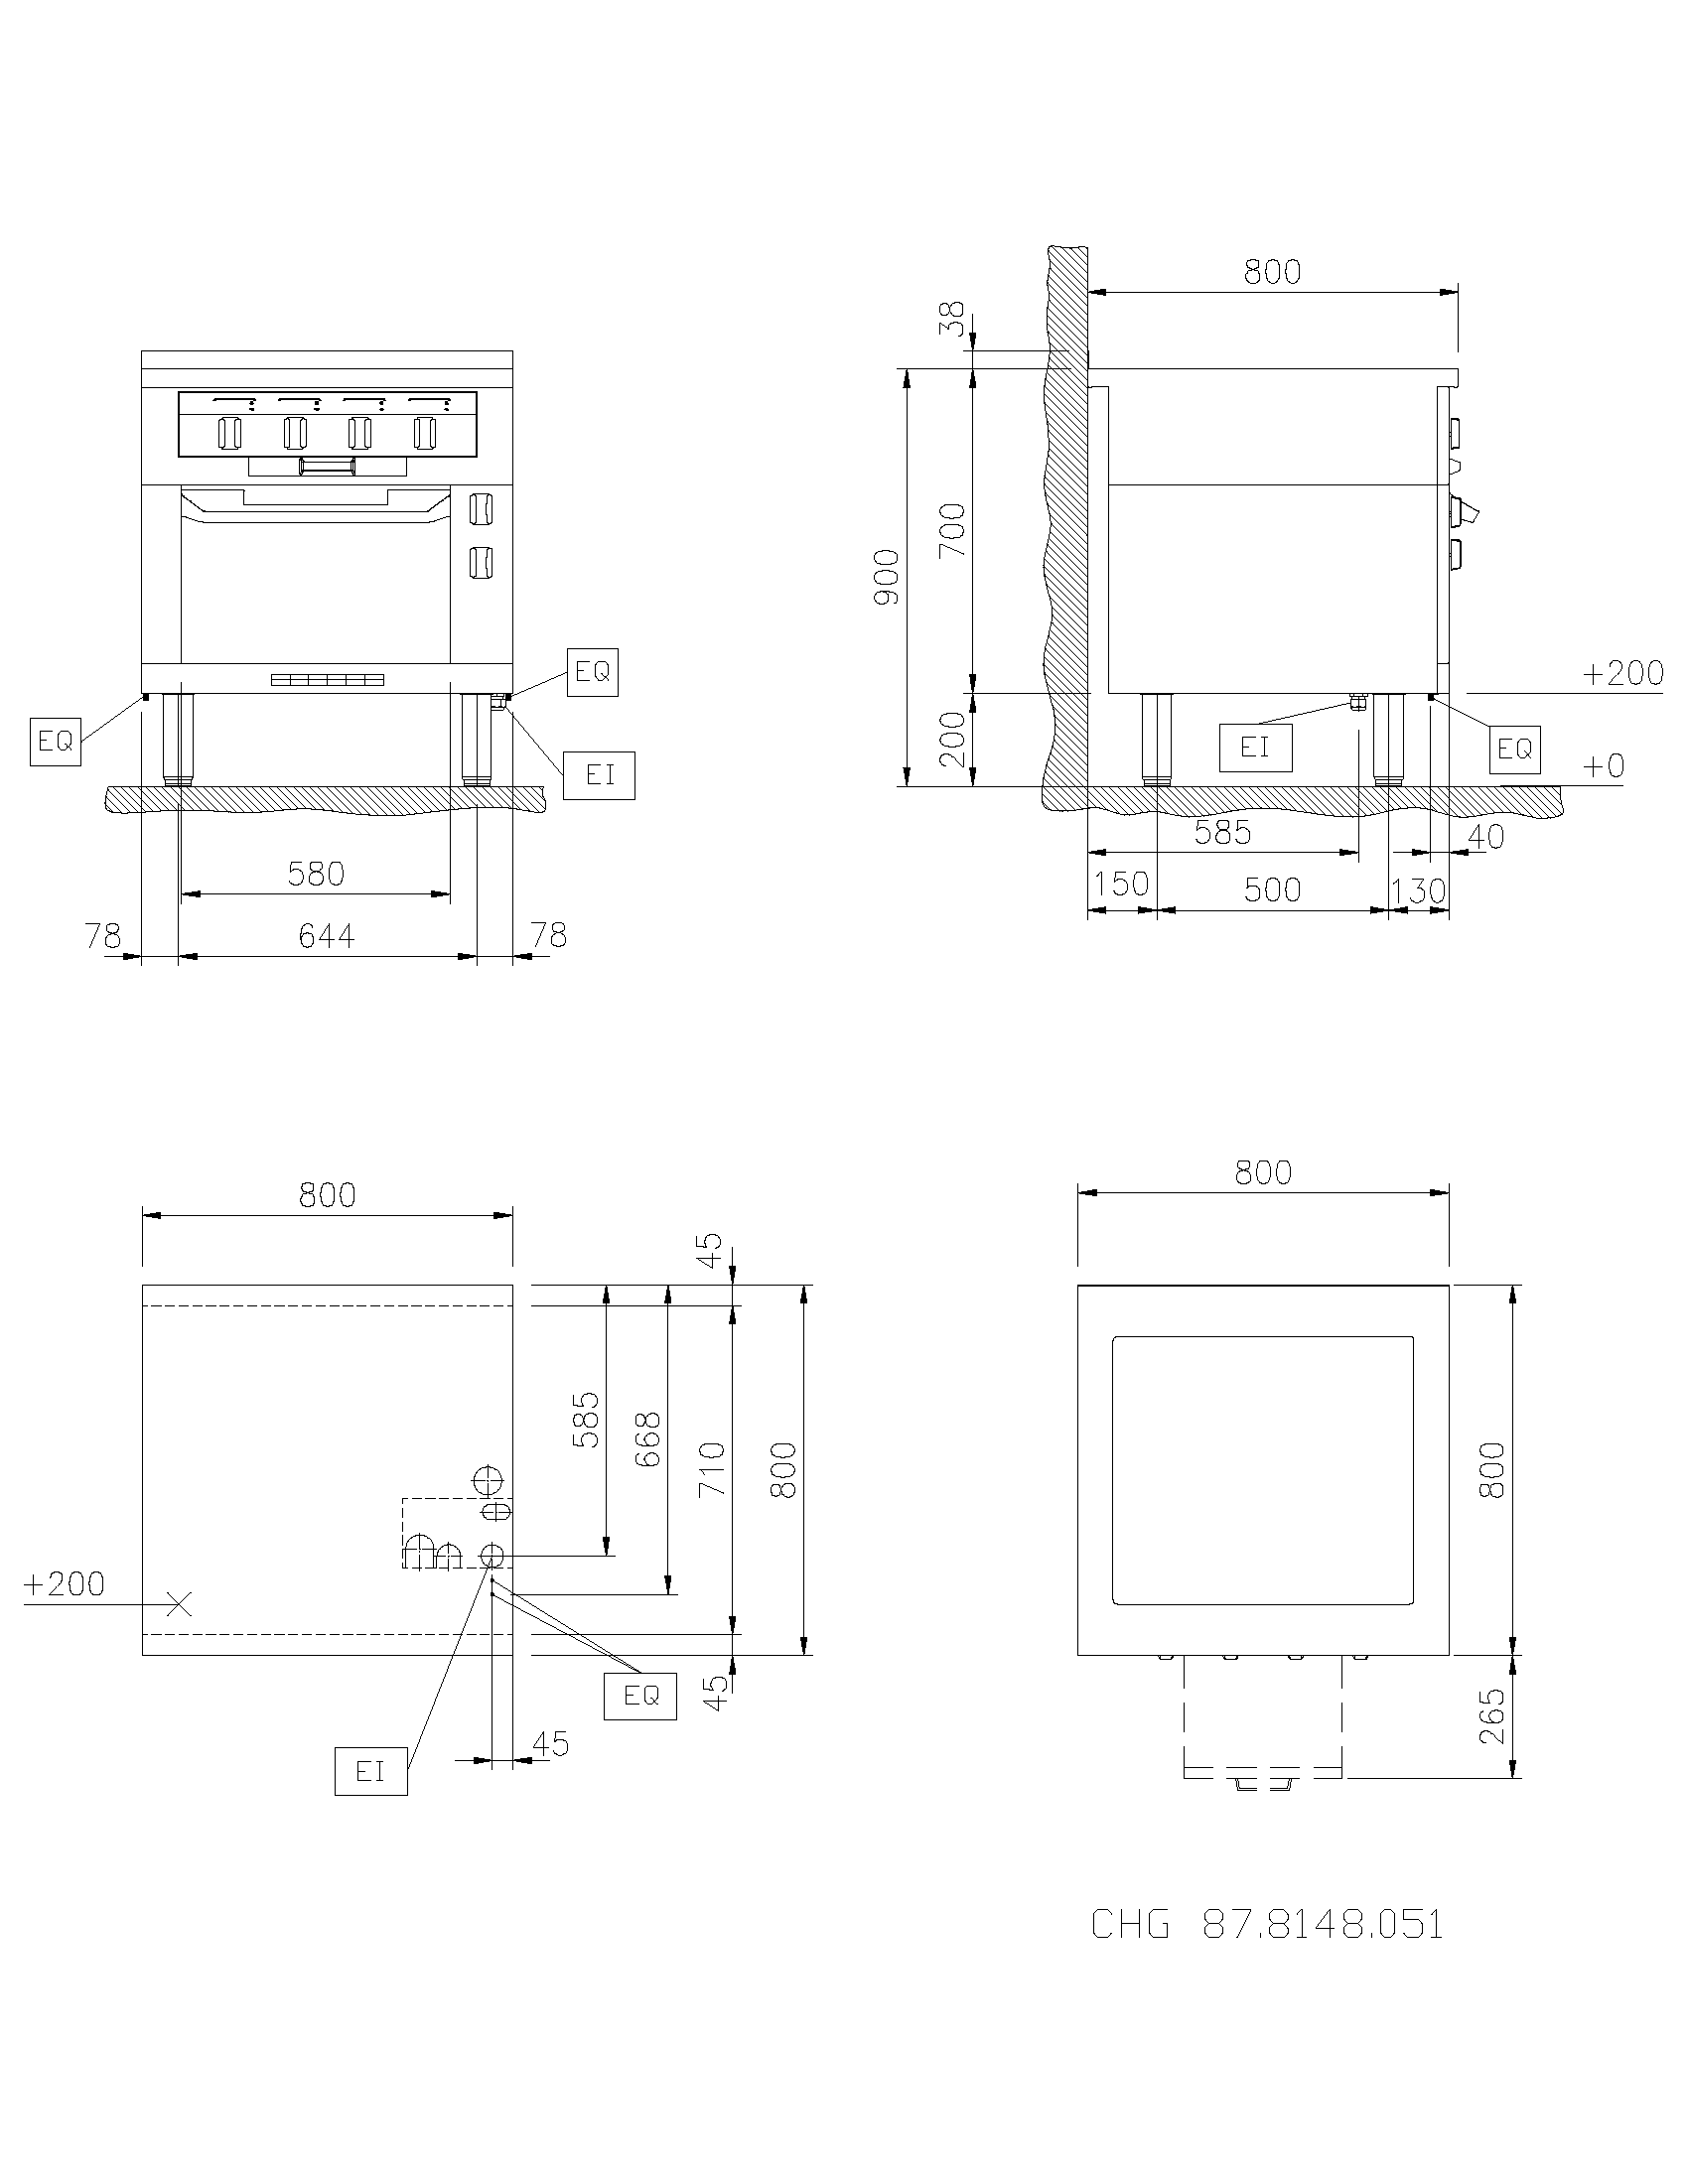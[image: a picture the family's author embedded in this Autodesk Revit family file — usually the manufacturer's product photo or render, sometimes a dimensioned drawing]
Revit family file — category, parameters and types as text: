
# Revit family: QF_ELECTROLUXPROFESSIONAL_588462_MALSECH4AO
name_source: partatom
category: Attrezzature speciali
units: mm (PartAtom-declared; Revit-internal decimal feet)

## family parameters
Basato su piano di lavoro = No
Condiviso = No
Punto di calcolo locali = No
Quota connettore circolare = Usa diametro
Sempre verticale = Sì
Taglio con vuoti quando caricato = No
Tipo di parte = Normale

## types (1)
- Standard
    Accessory = Sì
    Cold Water Size = 0"
    Compressed Air Pressure = 0.00 psi
    Compressed Air Size = 0"
    Compressed Air Volume = 0 GPM
    Condensate Return Size = 0"
    Cycle = 50 Hz
    Depth Actual = 800 mm  [stored 2.62467 ft]
    Descrizione = EL.SOLID T,ECO,WARM.C.PASS,2S,800X800X7
    Direct Waste Size = 0"
    Gas Input Pressure = 0.0
    Gas KW = 0
    Gas Size = 0"
    HP = 19.2 HP
    Height Actual = 700 mm  [stored 2.29659 ft]
    Hot Water Size = 0"
    Item Number = 588462
    Length Actual = 800 mm  [stored 2.62467 ft]
    Modello = MALSECH4AO
    Phase = 3
    Produttore = Electrolux Professional
    Prospetto di default = 0 mm  [stored 0 ft]
    Refrigerant Compressor Remote = Sì
    Refrigeration Liquid Line Size = 0 mm  [stored 0 ft]
    Refrigeration Suction Line Size = 0 mm  [stored 0 ft]
    Steam Consumption per Hour = 0
    Steam Supply Maximum Pressure = 0.00 psi
    Steam Supply Minimum Pressure = 0.00 psi
    Steam Supply Size = 0"
    URL = https://www.electroluxprofessional.com
    URL Manufacturer = https://www.electroluxprofessional.com
    Volts = 400 V
    Watts = 14300 W
    Weight = 147.00 kg

note: source unit labels omitted for Gas Input Pressure — the stored unit's dimension contradicts the parameter name (converter mislabeling)

note: [stored X ft] marks values corroborated as IEEE doubles in the binary element streams (Revit-internal decimal feet)

## geometry (parser evidence)
native form markers: Blend x10, Sweep x11
no freeform markers — native parametric forms only
